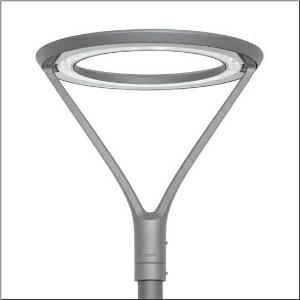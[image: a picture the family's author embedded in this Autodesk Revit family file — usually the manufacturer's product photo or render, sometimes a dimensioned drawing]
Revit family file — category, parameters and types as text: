
# Revit family: dl_r__20___pl1_2s_5xa512832s008p_c84b
name_source: partatom
category: Lighting Fixtures
units: mm (PartAtom-declared; Revit-internal decimal feet)

## family parameters
Cut with Voids When Loaded = No
Host = Face
Light Source = No
Part Type = Normal
Room Calculation Point = No
Round Connector Dimension = Use Diameter
Shared = No

## types (1)
- --- (1 x LED, 4250 lm, 43.6 W, 2200K)
    Apparent Load = 44 VA
    CIE Flux Codes = 33 78 99 100 100
    Color Rendering = 70
    Color Temperature = 2200K
    Default Elevation = 1800 mm
    Description = DL® 20, mast luminaire, primary light control with reflector, highly specular, primary optical cover: cover, of toughened safety glass of clear glass with excellent transmission level, light distribution: PL1.2s, light emission: direct distribution, primary light characteristic: symmetric, installation type: post-top, LED, High Power LED, rated luminous flux: 4.210lm, luminous efficacy: 80lm/W, light colour: 722, colour temperature: 2200K, control gear: Plus, control: flexible luminous flux parameterisation, time-dependent luminous flux control, constant luminous flux control, digital communication interface, power reduction, overheat protection, electronic power reduction, mains connection: 230..240V, 50/60Hz, connection cable pre-assembled, cable length: 5m, start of lifetime: 53W, end of service life: 54W, reduction: 24W, luminaire housing, upper part, of cast aluminium, powder-coated, Siteco® metallic grey (DB 702S), diameter: 690mm, height: 690mm, spigot size: 76mm (post-top), mounting height: 4..6m, luminaire housing, of cast aluminium, powder-coated, Siteco® metallic grey (DB 702S), equipment: Power, protection rating (complete): IP66, insulation class (complete): insulation class II (safety insulation), certification: CE, ENEC, VDE, impact resistance: IK08, permissible operating ambient temperature: -25..+30°C, standard-compliant lighting for roads and squares, packaging unit: 1 piece

Light Distribution: PL1.2s
    Height = 690 mm
    Lamp = 1 x LED
    Lamp Light Flux = 4250 lm
    Lamp Power = 43.6 W
    Lamp count = 1
    Length = 690 mm
    Luminous efficacy = 97 lm/W
    Manufacturer = Siteco
    ModVariant = No
    Model = 5XA512832S008P
    Number of Poles = 1
    OnlyDefault = Yes
    Power Factor = 1
    Product Name = DL® 20 | PL1.2s
    Product group = mast luminaire | pylon top
    ProductGroupID = 6100
    Protection Class = Protection class II
    Protection Degree = IP 66
    RLX_Detail_Level = 1
    RLX_Emergency_Light_Flux = 0 lm
    RLX_Emergency_Type = 0
    RLX_Emergency_Type_DB = No
    RlxData = <blob elided: 204413 chars, md5=76b5bbcb>
    Socket = socket
    Standby Power = 0 W
    System Light Flux = 4250 lm
    System Power = 44 W
    Type Comments = factory setting: luminous flux: 100 % | dim-lin: 254 | 587 mA
    Type Image = l_1006001.jpg
    URL = http://relux.com
    VarID = @adj_076976
    Voltage = 0 V
    Weight = 0.00 kg
    Width = 0 mm  [stored 0 ft]

note: [stored X ft] marks values corroborated as IEEE doubles in the binary element streams (Revit-internal decimal feet)

## geometry (parser evidence)
native form markers: Blend x4, Sweep x9
no freeform markers — native parametric forms only
